# Revit family: NLRS_27_GM_LIB_GBB_MR
name_source: partatom
category: Generic Models
units: mm (PartAtom-declared; Revit-internal decimal feet)

## family parameters
Can host rebar = No
Cut with Voids When Loaded = Yes
Part Type = Normal
Room Calculation Point = No
Round Connector Dimension = Use Diameter
Shared = No

## types (4) — shared parameters
Assembly Code = 27.16
Description = GBB Goot
IfcExportAs = IfcFlowsegment
Manufacturer = Meilof Riks bv
NLRS_C_Materiaal = RAL 9010 MR
Type Image = <None>
URL = https://www.meilofriks.nl
Vorm_Goot_L = 01 : 2_←_Hoek_L
Vorm_Goot_L-R = 01 : 4_↔_Hoek_L-R
Vorm_Goot_R = 01 : 3_→_Hoek_R
zero-valued in all types: Default Elevation

## per-type parameters (varying)
| type | GBB_hoogte | Model |
| 2-GBB 145 | 245 mm  [stored 0.803806 ft] | GBB 145 |
| 1-GBB 95 | 95 mm | GBB 95 |
| 3-GBB 195 | 195 mm  [stored 0.639764 ft] | GBB 195 |
| 4-GBB 245 | 245 mm  [stored 0.803806 ft] | GBB 245 |

note: [stored X ft] marks values corroborated as IEEE doubles in the binary element streams (Revit-internal decimal feet)

## geometry (parser evidence)
native form markers: Sweep x19
no freeform markers — native parametric forms only
